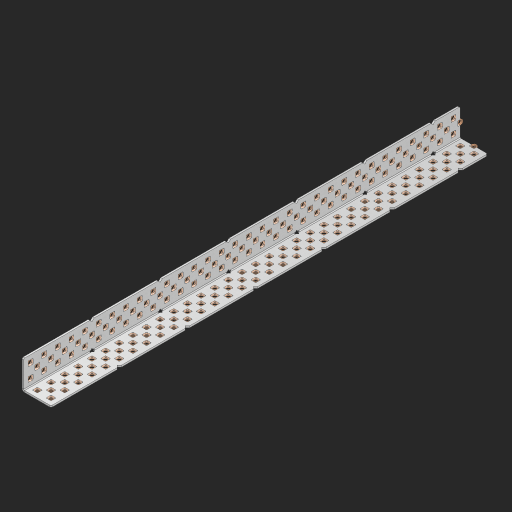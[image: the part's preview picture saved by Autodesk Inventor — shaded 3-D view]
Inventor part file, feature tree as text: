
AUTODESK INVENTOR PART (.ipt)
format: ipt  version: 2023 (Build 270158000, 158)  size: 2,197,504 bytes
history: native  units: in
note: dims shown in document units (in); Inventor stores cm internally (conversion verified against a paired STEP export)
features: other x198, extrude x190, sheet_metal_op x8, sketch x7, pattern_linear x2, mirror x1, chamfer x1
ambient origin geometry x8: Origin, YZ Plane, XZ Plane, XY Plane, X Axis, Y Axis, Z Axis, Center Point
bodies: Solid1 (feature_tree), Body (feature_tree)
feature tree (407):
  sheet_metal_op  "Flanges"
  sheet_metal_op  "Body Pattern"
  pattern_linear  "Center Pattern"  Spacing1=1.0in  [1 undecoded]
  other  "Arc Length"
  pattern_linear  "Notch Pattern"  Spacing1=0.25in  [1 undecoded]
  other  "Diagonal Plane"
  mirror  "Everything Mirrored"
  chamfer  "End Chamfer"
  sketch  "Sketch1"  dims[d0=1.0in]
  other  "Plate1"
  sketch  "Sketch2"  dims[d1=16.0in]
  other  "Plate2"
  sheet_metal_op  "Bend1"
  sheet_metal_op  "Corner1"
  sketch  "Sketch8"  dims[d2=0.0625in]
  sketch  "Sketch9"  dims[d3=0.0625in]
  other  "Srf91"
  sheet_metal_op  "Body Pattern Sketch"
  other  "Srf92"
  sketch  "Sketch13"  dims[d4=0.0312in]
  sketch  "Sketch15"  dims[d5=0.125in]
  sketch  "Sketch16"  dims[d6=0.0625in d7=1.0in d8=90.0deg d9=0.0312in d10=0.25in d11=0.0625in d12=0.0625in d49=0.182in d50=0.02in d52=0.25in d53=0.0625in d54=0.0in d55=0.172in d56=1.0in d57=0.0in d60=12.5984in d62=0.5in d63=0.7874in d65=0.5in d85=0.1473in d86=0.1782in d89=0.0625in d90=0.0in d91=0.04in d92=0.0491in d95=2.5in d96=0.04in d97=0.25in d98=45.0deg d99=0.25in d106=0.182in d107=0.02in d108=0.5in d110=0.0625in d111=0.0in d112=0.172in d113=0.5in d114=0.0in d117=0.5in d123=0.25in d125=0.25in d126=0.0491in d127=0.1473in d128=0.08in d129=0.04in d130=2.5in]
  other  "Srf786"
  other  "Srf856"
  other  "Srf857"
  other  "Srf858"
  other  "Srf859"
  other  "Srf860"
  other  "Srf861"
  other  "Srf889"
  other  "Srf890"
  other  "Srf891"
  other  "Srf1275"
  other  "Srf1276"
  other  "Srf1278"
  other  "Srf1279"
  other  "Srf1280"
  other  "Srf1281"
  other  "Srf1282"
  other  "Srf1283"
  other  "Srf1277"
  other  "Srf1285"
  other  "Srf1286"
  other  "Srf1287"
  other  "Srf1383"
  other  "Srf1384"
  other  "Srf1385"
  other  "Srf1386"
  other  "Srf1387"
  other  "Srf1388"
  other  "Srf1389"
  other  "Srf1390"
  other  "Srf1391"
  other  "Srf1392"
  other  "Srf1393"
  other  "Srf1394"
  other  "Srf1395"
  other  "Srf1396"
  other  "Srf1397"
  other  "Srf1398"
  other  "Srf1399"
  other  "Srf1400"
  other  "Srf1401"
  other  "Srf1402"
  other  "Srf1403"
  other  "Srf1404"
  other  "Srf1405"
  other  "Srf1406"
  other  "Srf1407"
  other  "Srf1408"
  other  "Srf1409"
  other  "Srf1410"
  other  "Srf1411"
  other  "Srf1412"
  other  "Srf1413"
  other  "Srf1414"
  other  "Srf1415"
  other  "Srf1416"
  other  "Srf1417"
  other  "Srf1418"
  other  "Srf1419"
  other  "Srf1420"
  other  "Srf1421"
  other  "Srf1422"
  other  "Srf1423"
  other  "Srf1424"
  other  "Srf1425"
  other  "Srf1426"
  other  "Srf1427"
  other  "Srf1428"
  other  "Srf1429"
  other  "Srf1430"
  other  "Srf1431"
  other  "Srf1432"
  other  "Srf1433"
  other  "Srf1434"
  other  "Srf1435"
  other  "Srf1436"
  other  "Srf1437"
  other  "Srf1438"
  other  "Srf1445"
  other  "Srf1446"
  other  "Srf1447"
  other  "Srf1448"
  other  "Srf1449"
  other  "Srf1450"
  other  "Srf1451"
  other  "Srf1452"
  other  "Srf1453"
  other  "Srf1454"
  other  "Srf1455"
  other  "Srf1456"
  other  "Srf1457"
  other  "Srf1458"
  other  "Srf1459"
  other  "Srf1460"
  other  "Srf1461"
  other  "Srf1462"
  other  "Srf1463"
  other  "Srf1464"
  other  "Srf1465"
  other  "Srf1466"
  other  "Srf1467"
  other  "Srf1468"
  other  "Srf1469"
  other  "Srf1470"
  other  "Srf1471"
  other  "Srf1472"
  other  "Srf1475"
  other  "Srf1476"
  other  "Srf1477"
  other  "Srf1478"
  other  "Srf1479"
  other  "Srf1480"
  other  "Srf1481"
  other  "Srf1482"
  other  "Srf1483"
  other  "Srf1484"
  other  "Srf1485"
  other  "Srf1486"
  other  "Srf1487"
  other  "Srf1488"
  other  "Srf1489"
  other  "Srf1490"
  other  "Srf1491"
  other  "Srf1492"
  other  "Srf1493"
  other  "Srf1494"
  other  "Srf1495"
  other  "Srf1496"
  other  "Srf1497"
  other  "Srf1498"
  other  "Srf1499"
  other  "Srf1500"
  other  "Srf1501"
  other  "Srf1502"
  other  "Srf1503"
  other  "Srf1504"
  other  "Srf1505"
  other  "Srf1506"
  other  "Srf1507"
  other  "Srf1508"
  other  "Srf1509"
  other  "Srf1510"
  other  "Srf1511"
  other  "Srf1512"
  other  "Srf1513"
  other  "Srf1514"
  other  "Srf1515"
  other  "Srf1516"
  other  "Srf1517"
  other  "Srf1518"
  other  "Srf1519"
  other  "Srf1520"
  other  "Srf1521"
  other  "Srf1522"
  other  "Srf1523"
  other  "Srf1524"
  other  "Srf1525"
  other  "Srf1526"
  other  "Srf1527"
  other  "Srf1528"
  other  "Srf1529"
  other  "Srf1530"
  other  "Srf1537"
  other  "Srf1538"
  other  "Srf1539"
  other  "Srf1540"
  other  "Srf1541"
  other  "Srf1542"
  other  "Srf1543"
  other  "Srf1544"
  other  "Srf1545"
  other  "Srf1546"
  other  "Srf1547"
  other  "Srf1548"
  other  "Srf1549"
  other  "Srf1550"
  other  "Srf1551"
  other  "Srf1552"
  other  "Srf1553"
  other  "Srf1554"
  other  "Srf1555"
  other  "Srf1556"
  other  "Srf1557"
  other  "Srf1558"
  other  "Srf1559"
  other  "Srf1560"
  other  "Srf1561"
  other  "Srf1562"
  other  "Srf1563"
  other  "Srf1564"
  sheet_metal_op  "Body Stamp"
  sheet_metal_op  "Body Circle"
  other  "Center Stamp"
  other  "Center Circle"
  sheet_metal_op  "Notch"
  extrude  "ExtrusionSrf92"  Depth=0.0625in
  extrude  "ExtrusionSrf856"  Depth=0.0625in
  extrude  "ExtrusionSrf857"  Depth=0.182in
  extrude  "ExtrusionSrf858"  Depth=0.02in
  extrude  "ExtrusionSrf859"  Depth=0.25in
  extrude  "ExtrusionSrf860"  Depth=0.0625in
  extrude  "ExtrusionSrf861"  TaperAngle=0.0deg  [1 undecoded]
  extrude  "ExtrusionSrf889"  Depth=2.5in
  extrude  "ExtrusionSrf890"  Depth=1.0in TaperAngle=0.0deg
  extrude  "ExtrusionSrf891"  Depth=2.5in
  extrude  "ExtrusionSrf1275"  Depth=0.5in
  extrude  "ExtrusionSrf1276"  Depth=2.5in
  extrude  "ExtrusionSrf1277"  Depth=2.5in
  extrude  "ExtrusionSrf1278"  Depth=0.0625in
  extrude  "ExtrusionSrf1279"  Depth=2.5in TaperAngle=0.0deg
  extrude  "ExtrusionSrf1280"  Depth=2.5in
  extrude  "ExtrusionSrf1281"  Depth=0.25in TaperAngle=45.0deg
  extrude  "ExtrusionSrf1282"  Depth=0.25in
  extrude  "ExtrusionSrf1345"  Depth=0.182in
  extrude  "ExtrusionSrf1346"  Depth=0.02in
  extrude  "ExtrusionSrf1347"  Depth=0.5in
  extrude  "ExtrusionSrf1348"  Depth=0.0625in
  extrude  "ExtrusionSrf1383"  TaperAngle=0.0deg  [1 undecoded]
  extrude  "ExtrusionSrf1384"  Depth=2.5in
  extrude  "ExtrusionSrf1385"  Depth=0.5in TaperAngle=0.0deg
  extrude  "ExtrusionSrf1386"  Depth=0.5in
  extrude  "ExtrusionSrf1387"  Depth=0.25in
  extrude  "ExtrusionSrf1388"  Depth=0.25in
  extrude  "ExtrusionSrf1389"  Depth=2.5in
  extrude  "ExtrusionSrf1390"  Depth=2.5in
  extrude  "ExtrusionSrf1391"  Depth=2.5in
  extrude  "ExtrusionSrf1392"  Depth=2.5in
  extrude  "ExtrusionSrf1393"  Depth=2.5in
  extrude  "ExtrusionSrf1394"  [1 undecoded]
  extrude  "ExtrusionSrf1395"  [1 undecoded]
  extrude  "ExtrusionSrf1396"  [1 undecoded]
  extrude  "ExtrusionSrf1397"  [1 undecoded]
  extrude  "ExtrusionSrf1398"  [1 undecoded]
  extrude  "ExtrusionSrf1399"  [1 undecoded]
  extrude  "ExtrusionSrf1400"  [1 undecoded]
  extrude  "ExtrusionSrf1401"  [1 undecoded]
  extrude  "ExtrusionSrf1402"  [1 undecoded]
  extrude  "ExtrusionSrf1403"  [1 undecoded]
  extrude  "ExtrusionSrf1404"  [1 undecoded]
  extrude  "ExtrusionSrf1405"  [1 undecoded]
  extrude  "ExtrusionSrf1406"  [1 undecoded]
  extrude  "ExtrusionSrf1407"  [1 undecoded]
  extrude  "ExtrusionSrf1408"  [1 undecoded]
  extrude  "ExtrusionSrf1409"  [1 undecoded]
  extrude  "ExtrusionSrf1410"  [1 undecoded]
  extrude  "ExtrusionSrf1411"  [1 undecoded]
  extrude  "ExtrusionSrf1412"  [1 undecoded]
  extrude  "ExtrusionSrf1413"  [1 undecoded]
  extrude  "ExtrusionSrf1414"  [1 undecoded]
  extrude  "ExtrusionSrf1415"  [1 undecoded]
  extrude  "ExtrusionSrf1416"  [1 undecoded]
  extrude  "ExtrusionSrf1417"  [1 undecoded]
  extrude  "ExtrusionSrf1418"  [1 undecoded]
  extrude  "ExtrusionSrf1419"  [1 undecoded]
  extrude  "ExtrusionSrf1420"  [1 undecoded]
  extrude  "ExtrusionSrf1421"  [1 undecoded]
  extrude  "ExtrusionSrf1422"  [1 undecoded]
  extrude  "ExtrusionSrf1423"  [1 undecoded]
  extrude  "ExtrusionSrf1424"  [1 undecoded]
  extrude  "ExtrusionSrf1425"  [1 undecoded]
  extrude  "ExtrusionSrf1426"  [1 undecoded]
  extrude  "ExtrusionSrf1427"  [1 undecoded]
  extrude  "ExtrusionSrf1428"  [1 undecoded]
  extrude  "ExtrusionSrf1429"  [1 undecoded]
  extrude  "ExtrusionSrf1430"  [1 undecoded]
  extrude  "ExtrusionSrf1431"  [1 undecoded]
  extrude  "ExtrusionSrf1432"  [1 undecoded]
  extrude  "ExtrusionSrf1433"  [1 undecoded]
  extrude  "ExtrusionSrf1434"  [1 undecoded]
  extrude  "ExtrusionSrf1435"  [1 undecoded]
  extrude  "ExtrusionSrf1436"  [1 undecoded]
  extrude  "ExtrusionSrf1437"  [1 undecoded]
  extrude  "ExtrusionSrf1438"  [1 undecoded]
  extrude  "ExtrusionSrf1445"  [1 undecoded]
  extrude  "ExtrusionSrf1446"  [1 undecoded]
  extrude  "ExtrusionSrf1447"  [1 undecoded]
  extrude  "ExtrusionSrf1448"  [1 undecoded]
  extrude  "ExtrusionSrf1449"  [1 undecoded]
  extrude  "ExtrusionSrf1450"  [1 undecoded]
  extrude  "ExtrusionSrf1451"  [1 undecoded]
  extrude  "ExtrusionSrf1452"  [1 undecoded]
  extrude  "ExtrusionSrf1453"  [1 undecoded]
  extrude  "ExtrusionSrf1454"  [1 undecoded]
  extrude  "ExtrusionSrf1455"  [1 undecoded]
  extrude  "ExtrusionSrf1456"  [1 undecoded]
  extrude  "ExtrusionSrf1457"  [1 undecoded]
  extrude  "ExtrusionSrf1458"  [1 undecoded]
  extrude  "ExtrusionSrf1459"  [1 undecoded]
  extrude  "ExtrusionSrf1460"  [1 undecoded]
  extrude  "ExtrusionSrf1461"  [1 undecoded]
  extrude  "ExtrusionSrf1462"  [1 undecoded]
  extrude  "ExtrusionSrf1463"  [1 undecoded]
  extrude  "ExtrusionSrf1464"  [1 undecoded]
  extrude  "ExtrusionSrf1465"  [1 undecoded]
  extrude  "ExtrusionSrf1466"  [1 undecoded]
  extrude  "ExtrusionSrf1467"  [1 undecoded]
  extrude  "ExtrusionSrf1468"  [1 undecoded]
  extrude  "ExtrusionSrf1469"  [1 undecoded]
  extrude  "ExtrusionSrf1470"  [1 undecoded]
  extrude  "ExtrusionSrf1471"  [1 undecoded]
  extrude  "ExtrusionSrf1472"  [1 undecoded]
  extrude  "ExtrusionSrf1475"  [1 undecoded]
  extrude  "ExtrusionSrf1476"  [1 undecoded]
  extrude  "ExtrusionSrf1477"  [1 undecoded]
  extrude  "ExtrusionSrf1478"  [1 undecoded]
  extrude  "ExtrusionSrf1479"  [1 undecoded]
  extrude  "ExtrusionSrf1480"  [1 undecoded]
  extrude  "ExtrusionSrf1481"  [1 undecoded]
  extrude  "ExtrusionSrf1482"  [1 undecoded]
  extrude  "ExtrusionSrf1483"  [1 undecoded]
  extrude  "ExtrusionSrf1484"  [1 undecoded]
  extrude  "ExtrusionSrf1485"  [1 undecoded]
  extrude  "ExtrusionSrf1486"  [1 undecoded]
  extrude  "ExtrusionSrf1487"  [1 undecoded]
  extrude  "ExtrusionSrf1488"  [1 undecoded]
  extrude  "ExtrusionSrf1489"  [1 undecoded]
  extrude  "ExtrusionSrf1490"  [1 undecoded]
  extrude  "ExtrusionSrf1491"  [1 undecoded]
  extrude  "ExtrusionSrf1492"  [1 undecoded]
  extrude  "ExtrusionSrf1493"  [1 undecoded]
  extrude  "ExtrusionSrf1494"  [1 undecoded]
  extrude  "ExtrusionSrf1495"  [1 undecoded]
  extrude  "ExtrusionSrf1496"  [1 undecoded]
  extrude  "ExtrusionSrf1497"  [1 undecoded]
  extrude  "ExtrusionSrf1498"  [1 undecoded]
  extrude  "ExtrusionSrf1499"  [1 undecoded]
  extrude  "ExtrusionSrf1500"  [1 undecoded]
  extrude  "ExtrusionSrf1501"  [1 undecoded]
  extrude  "ExtrusionSrf1502"  [1 undecoded]
  extrude  "ExtrusionSrf1503"  [1 undecoded]
  extrude  "ExtrusionSrf1504"  [1 undecoded]
  extrude  "ExtrusionSrf1505"  [1 undecoded]
  extrude  "ExtrusionSrf1506"  [1 undecoded]
  extrude  "ExtrusionSrf1507"  [1 undecoded]
  extrude  "ExtrusionSrf1508"  [1 undecoded]
  extrude  "ExtrusionSrf1509"  [1 undecoded]
  extrude  "ExtrusionSrf1510"  [1 undecoded]
  extrude  "ExtrusionSrf1511"  [1 undecoded]
  extrude  "ExtrusionSrf1512"  [1 undecoded]
  extrude  "ExtrusionSrf1513"  [1 undecoded]
  extrude  "ExtrusionSrf1514"  [1 undecoded]
  extrude  "ExtrusionSrf1515"  [1 undecoded]
  extrude  "ExtrusionSrf1516"  [1 undecoded]
  extrude  "ExtrusionSrf1517"  [1 undecoded]
  extrude  "ExtrusionSrf1518"  [1 undecoded]
  extrude  "ExtrusionSrf1519"  [1 undecoded]
  extrude  "ExtrusionSrf1520"  [1 undecoded]
  extrude  "ExtrusionSrf1521"  [1 undecoded]
  extrude  "ExtrusionSrf1522"  [1 undecoded]
  extrude  "ExtrusionSrf1523"  [1 undecoded]
  extrude  "ExtrusionSrf1524"  [1 undecoded]
  extrude  "ExtrusionSrf1525"  [1 undecoded]
  extrude  "ExtrusionSrf1526"  [1 undecoded]
  extrude  "ExtrusionSrf1527"  [1 undecoded]
  extrude  "ExtrusionSrf1528"  [1 undecoded]
  extrude  "ExtrusionSrf1529"  [1 undecoded]
  extrude  "ExtrusionSrf1530"  [1 undecoded]
  extrude  "ExtrusionSrf1537"  [1 undecoded]
  extrude  "ExtrusionSrf1538"  [1 undecoded]
  extrude  "ExtrusionSrf1539"  [1 undecoded]
  extrude  "ExtrusionSrf1540"  [1 undecoded]
  extrude  "ExtrusionSrf1541"  [1 undecoded]
  extrude  "ExtrusionSrf1542"  [1 undecoded]
  extrude  "ExtrusionSrf1543"  [1 undecoded]
  extrude  "ExtrusionSrf1544"  [1 undecoded]
  extrude  "ExtrusionSrf1545"  [1 undecoded]
  extrude  "ExtrusionSrf1546"  [1 undecoded]
  extrude  "ExtrusionSrf1547"  [1 undecoded]
  extrude  "ExtrusionSrf1548"  [1 undecoded]
  extrude  "ExtrusionSrf1549"  [1 undecoded]
  extrude  "ExtrusionSrf1550"  [1 undecoded]
  extrude  "ExtrusionSrf1551"  [1 undecoded]
  extrude  "ExtrusionSrf1552"  [1 undecoded]
  extrude  "ExtrusionSrf1553"  [1 undecoded]
  extrude  "ExtrusionSrf1554"  [1 undecoded]
  extrude  "ExtrusionSrf1555"  [1 undecoded]
  extrude  "ExtrusionSrf1556"  [1 undecoded]
  extrude  "ExtrusionSrf1557"  [1 undecoded]
  extrude  "ExtrusionSrf1558"  [1 undecoded]
  extrude  "ExtrusionSrf1559"  [1 undecoded]
  extrude  "ExtrusionSrf1560"  [1 undecoded]
  extrude  "ExtrusionSrf1561"  [1 undecoded]
  extrude  "ExtrusionSrf1562"  [1 undecoded]
  extrude  "ExtrusionSrf1563"  [1 undecoded]
  extrude  "ExtrusionSrf1564"  [1 undecoded]
note: 161 required parameter values undecoded (feature->parameter linkage not recoverable at this tier; creation-order binding heuristic only, values carry confidence <= 0.55)
